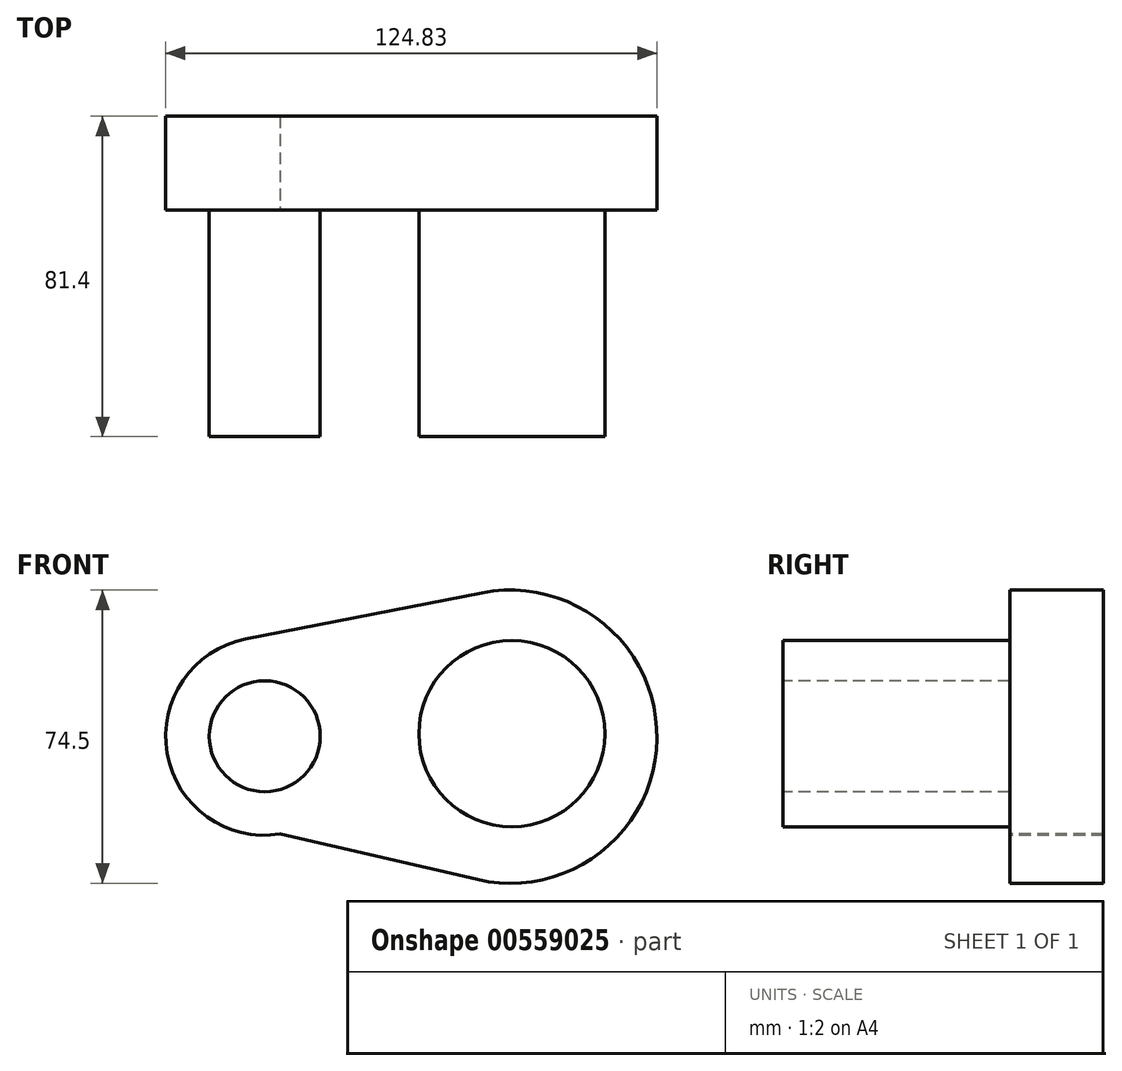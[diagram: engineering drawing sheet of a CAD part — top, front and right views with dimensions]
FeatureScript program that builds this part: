
annotation { "Feature Type Name" : "Feature", "Feature Type Description" : "" }
export const myFeature = defineFeature(function(context is Context, id is Id, definition is map)
    precondition{}
    {
        {
            var Q0;
            Q0=qCreatedBy(makeId("Front.planeOp"),FACE);
            var sketch = newSketch(context, id + "F0", { "sketchPlane" : qUnion([Q0])});
            skCircle(sketch, "E0", {"center": v(44.75, 32.59) * mm, "radius": 37.25 * mm});
            skCircle(sketch, "E1", {"center": v(-17.67, 32.7) * mm, "radius": 25.16 * mm});
            skLineSegment(sketch, "E2", {"start": v(-13.74, 7.85) * mm, "end": v(36.38, -3.7) * mm});
            skLineSegment(sketch, "E3", {"start": v(-22.5, 57.4) * mm, "end": v(37.6, 69.15) * mm});
            skSolve(sketch);
        }
        {
            var Q0;
            Q0=qCreatedBy(makeId("Front.planeOp"),FACE);
            var sketch = newSketch(context, id + "F1", { "sketchPlane" : qUnion([Q0])});
            skCircle(sketch, "E4", {"center": v(45.13, 33.36) * mm, "radius": 23.62 * mm});
            skCircle(sketch, "E5", {"center": v(-17.66, 32.7) * mm, "radius": 14.09 * mm});
            skSolve(sketch);
        }
        {
            var Q0;
            Q0 = qSketchRegion(id + "F1", true);
            var Q1;
            Q1 = qSketchRegion(id + "F0", true);
            extrude(context, id + "F2", {"entities" : qUnion([Q0, Q1]), "oppositeDirection" : true, "depth" : 23.8 * mm, "offsetDistance" : 25 * mm});
        }
        {
            var Q0;
            Q0 = qSketchRegion(id + "F1", true);
            extrude(context, id + "F3", {"entities" : qUnion([Q0]), "operationType" : NewBodyOperationType.ADD, "depth" : 57.6 * mm, "offsetDistance" : 25 * mm});
        }
    });
